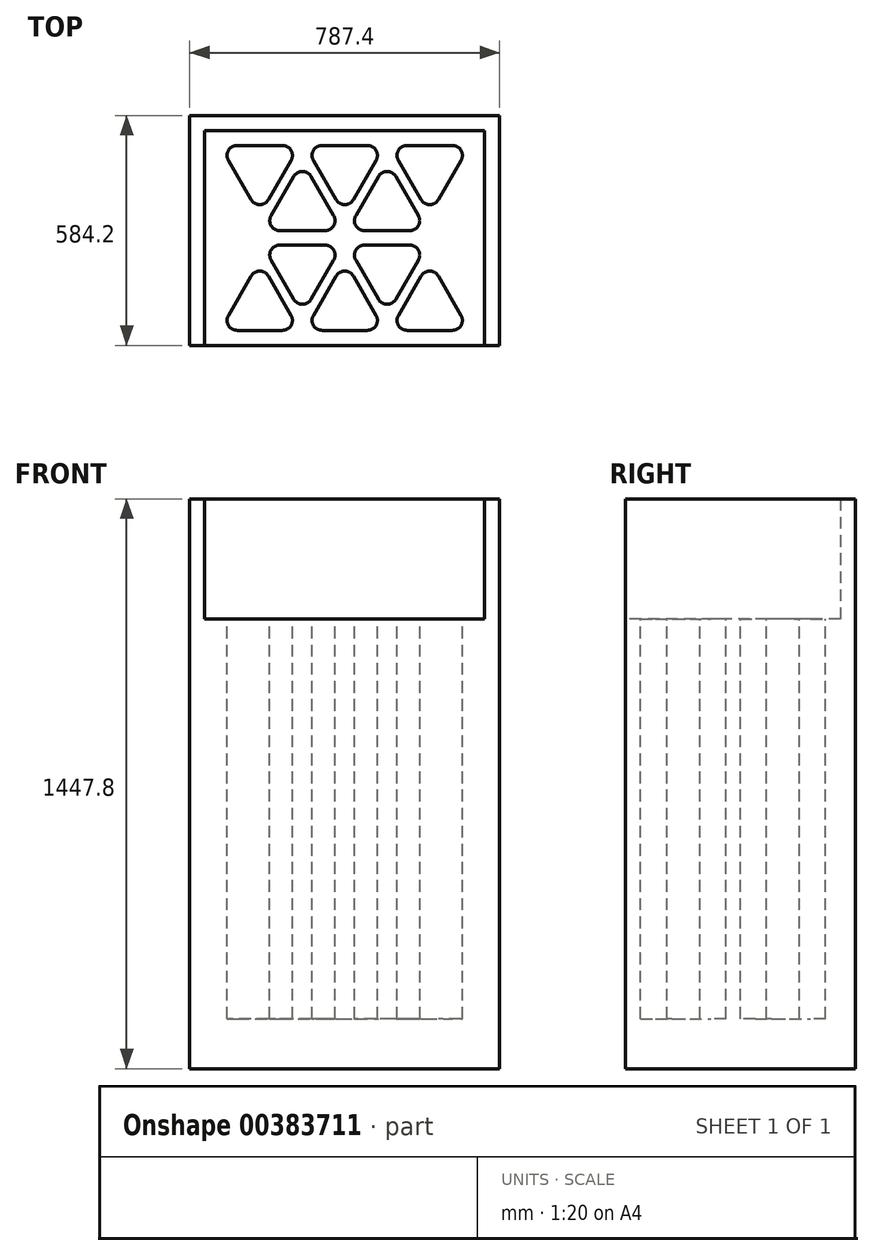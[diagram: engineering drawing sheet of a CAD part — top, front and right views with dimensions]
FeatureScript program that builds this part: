
annotation { "Feature Type Name" : "Feature", "Feature Type Description" : "" }
export const myFeature = defineFeature(function(context is Context, id is Id, definition is map)
    precondition{}
    {
        {
            var Q0;
            Q0=qCreatedBy(makeId("Top.planeOp"),FACE);
            var sketch = newSketch(context, id + "F0", { "sketchPlane" : qUnion([Q0])});
            skLineSegment(sketch, "E0.bottom", {"start": v(-70.95, -74.95) * mm, "end": v(716.45, -74.95) * mm});
            skLineSegment(sketch, "E0.top", {"start": v(-70.95, 509.25) * mm, "end": v(716.45, 509.25) * mm});
            skLineSegment(sketch, "E0.left", {"start": v(-70.95, -74.95) * mm, "end": v(-70.95, 509.25) * mm});
            skLineSegment(sketch, "E0.right", {"start": v(716.45, -74.95) * mm, "end": v(716.45, 509.25) * mm});
            skSolve(sketch);
        }
        {
            var Q0;
            Q0 = qSketchRegion(id + "F0", true);
            extrude(context, id + "F1", {"entities" : qUnion([Q0]), "depth" : 1447.8 * mm});
        }
        {
            var Q0;
            Q0=makeQuery(id+"F1.opExtrude","SWEPT_FACE",FACE,{"disambiguationData":[OSD([sQuery(id+"F0.wireOp",EDGE,"E0.bottom")])]});
            var sketch = newSketch(context, id + "F2", { "sketchPlane" : qUnion([Q0])});
            skLineSegment(sketch, "E1.bottom", {"start": v(-32.85, 1447.8) * mm, "end": v(678.35, 1447.8) * mm});
            skLineSegment(sketch, "E1.top", {"start": v(-32.85, 1143) * mm, "end": v(678.35, 1143) * mm});
            skLineSegment(sketch, "E1.left", {"start": v(-32.85, 1447.8) * mm, "end": v(-32.85, 1143) * mm});
            skLineSegment(sketch, "E1.right", {"start": v(678.35, 1447.8) * mm, "end": v(678.35, 1143) * mm});
            skSolve(sketch);
        }
        {
            var Q0;
            Q0 = qSketchRegion(id + "F2", true);
            extrude(context, id + "F3", {"entities" : qUnion([Q0]), "operationType" : NewBodyOperationType.REMOVE, "oppositeDirection" : true, "depth" : 546.1 * mm});
        }
        {
            var Q0;
            Q0=makeQuery(id+"F3.boolean.opBoolean","COPY",FACE,{"derivedFrom":makeQuery(id+"F3.opExtrude","SWEPT_FACE",FACE,{"disambiguationData":[OSD([sQuery(id+"F2.wireOp",EDGE,"E1.top")])]})});
            var sketch = newSketch(context, id + "F4", { "sketchPlane" : qUnion([Q0])});
            skLineSegment(sketch, "E2", {"start": v(49.24, -36.85) * mm, "end": v(164.45, -36.85) * mm});
            skLineSegment(sketch, "E3", {"start": v(186.45, 1.25) * mm, "end": v(128.84, 101.03) * mm});
            skLineSegment(sketch, "E4", {"start": v(84.85, 101.03) * mm, "end": v(27.24, 1.25) * mm});
            skPoint(sketch, "E5.visualSharp", {"position": v(106.85, 139.13) * mm});
            skArc(sketch, "E5.filletArc", {"start": v(128.84, 101.03) * mm, "mid": v(106.85, 113.73) * mm, "end": v(84.85, 101.03) * mm});
            skPoint(sketch, "E6.visualSharp", {"position": v(208.45, -36.85) * mm});
            skArc(sketch, "E6.filletArc", {"start": v(164.45, -36.85) * mm, "mid": v(186.45, -24.15) * mm, "end": v(186.45, 1.25) * mm});
            skPoint(sketch, "E7.visualSharp", {"position": v(5.25, -36.85) * mm});
            skArc(sketch, "E7.filletArc", {"start": v(27.24, 1.25) * mm, "mid": v(27.24, -24.15) * mm, "end": v(49.24, -36.85) * mm});
            skLineSegment(sketch, "E8.1.0.0", {"start": v(402.35, 1.25) * mm, "end": v(344.74, 101.03) * mm});
            skLineSegment(sketch, "E8.1.0.1", {"start": v(265.14, -36.85) * mm, "end": v(380.35, -36.85) * mm});
            skLineSegment(sketch, "E8.1.0.2", {"start": v(300.75, 101.03) * mm, "end": v(243.14, 1.25) * mm});
            skPoint(sketch, "E8.1.0.3", {"position": v(424.35, -36.85) * mm});
            skPoint(sketch, "E8.1.0.4", {"position": v(221.15, -36.85) * mm});
            skPoint(sketch, "E8.1.0.5", {"position": v(322.75, 139.13) * mm});
            skArc(sketch, "E8.1.0.6", {"start": v(344.74, 101.03) * mm, "mid": v(322.75, 113.73) * mm, "end": v(300.75, 101.03) * mm});
            skArc(sketch, "E8.1.0.7", {"start": v(380.35, -36.85) * mm, "mid": v(402.35, -24.15) * mm, "end": v(402.35, 1.25) * mm});
            skArc(sketch, "E8.1.0.8", {"start": v(243.14, 1.25) * mm, "mid": v(243.14, -24.15) * mm, "end": v(265.14, -36.85) * mm});
            skLineSegment(sketch, "E8.2.0.0", {"start": v(618.25, 1.25) * mm, "end": v(560.64, 101.03) * mm});
            skLineSegment(sketch, "E8.2.0.1", {"start": v(481.04, -36.85) * mm, "end": v(596.25, -36.85) * mm});
            skLineSegment(sketch, "E8.2.0.2", {"start": v(516.65, 101.03) * mm, "end": v(459.04, 1.25) * mm});
            skPoint(sketch, "E8.2.0.3", {"position": v(640.25, -36.85) * mm});
            skPoint(sketch, "E8.2.0.4", {"position": v(437.05, -36.85) * mm});
            skPoint(sketch, "E8.2.0.5", {"position": v(538.65, 139.13) * mm});
            skArc(sketch, "E8.2.0.6", {"start": v(560.64, 101.03) * mm, "mid": v(538.65, 113.73) * mm, "end": v(516.65, 101.03) * mm});
            skArc(sketch, "E8.2.0.7", {"start": v(596.25, -36.85) * mm, "mid": v(618.25, -24.15) * mm, "end": v(618.25, 1.25) * mm});
            skArc(sketch, "E8.2.0.8", {"start": v(459.04, 1.25) * mm, "mid": v(459.04, -24.15) * mm, "end": v(481.04, -36.85) * mm});
            skLineSegment(sketch, "E8.direction1", {"start": v(5.25, -36.85) * mm, "end": v(221.15, -36.85) * mm, "construction": true});
            skLineSegment(sketch, "E9", {"start": v(157.55, 179.9) * mm, "end": v(272.76, 179.9) * mm});
            skLineSegment(sketch, "E10", {"start": v(294.76, 141.8) * mm, "end": v(237.15, 42.02) * mm});
            skLineSegment(sketch, "E11", {"start": v(193.16, 42.02) * mm, "end": v(135.55, 141.8) * mm});
            skPoint(sketch, "E12.visualSharp", {"position": v(113.55, 179.9) * mm});
            skArc(sketch, "E12.filletArc", {"start": v(157.55, 179.9) * mm, "mid": v(135.55, 167.2) * mm, "end": v(135.55, 141.8) * mm});
            skPoint(sketch, "E13.visualSharp", {"position": v(316.75, 179.9) * mm});
            skArc(sketch, "E13.filletArc", {"start": v(294.76, 141.8) * mm, "mid": v(294.76, 167.2) * mm, "end": v(272.76, 179.9) * mm});
            skPoint(sketch, "E14.visualSharp", {"position": v(215.15, 3.92) * mm});
            skArc(sketch, "E14.filletArc", {"start": v(193.16, 42.02) * mm, "mid": v(215.15, 29.32) * mm, "end": v(237.15, 42.02) * mm});
            skLineSegment(sketch, "E15", {"start": v(322.75, 139.13) * mm, "end": v(322.75, 471.15) * mm, "construction": true});
            skArc(sketch, "E16.MirrorCS", {"start": v(487.94, 179.9) * mm, "mid": v(509.94, 167.2) * mm, "end": v(509.94, 141.8) * mm});
            skPoint(sketch, "E17.MirrorP", {"position": v(531.94, 179.9) * mm});
            skLineSegment(sketch, "E18.MirrorCS", {"start": v(452.34, 42.02) * mm, "end": v(509.94, 141.8) * mm});
            skArc(sketch, "E19.MirrorCS", {"start": v(452.34, 42.02) * mm, "mid": v(430.34, 29.32) * mm, "end": v(408.34, 42.02) * mm});
            skPoint(sketch, "E20.MirrorP", {"position": v(328.74, 179.9) * mm});
            skArc(sketch, "E21.MirrorCS", {"start": v(350.74, 141.8) * mm, "mid": v(350.74, 167.2) * mm, "end": v(372.73, 179.9) * mm});
            skLineSegment(sketch, "E22.MirrorCS", {"start": v(350.74, 141.8) * mm, "end": v(408.34, 42.02) * mm});
            skPoint(sketch, "E23.MirrorP", {"position": v(430.34, 3.92) * mm});
            skLineSegment(sketch, "E24.MirrorCS", {"start": v(487.94, 179.9) * mm, "end": v(372.73, 179.9) * mm});
            skLineSegment(sketch, "E25.MirrorCS", {"start": v(49.24, 433.05) * mm, "end": v(164.45, 433.05) * mm});
            skPoint(sketch, "E26.MirrorP", {"position": v(106.85, 257.07) * mm});
            skPoint(sketch, "E27.MirrorP", {"position": v(531.94, 216.3) * mm});
            skLineSegment(sketch, "E28.MirrorCS", {"start": v(618.25, 394.95) * mm, "end": v(560.64, 295.17) * mm});
            skArc(sketch, "E29.MirrorCS", {"start": v(193.16, 354.18) * mm, "mid": v(215.15, 366.88) * mm, "end": v(237.15, 354.18) * mm});
            skLineSegment(sketch, "E30.MirrorCS", {"start": v(481.04, 433.05) * mm, "end": v(596.25, 433.05) * mm});
            skLineSegment(sketch, "E31.MirrorCS", {"start": v(350.74, 254.4) * mm, "end": v(408.34, 354.18) * mm});
            skLineSegment(sketch, "E32.MirrorCS", {"start": v(193.16, 354.18) * mm, "end": v(135.55, 254.4) * mm});
            skPoint(sketch, "E33.MirrorP", {"position": v(640.25, 433.05) * mm});
            skArc(sketch, "E34.MirrorCS", {"start": v(452.34, 354.18) * mm, "mid": v(430.34, 366.88) * mm, "end": v(408.34, 354.18) * mm});
            skArc(sketch, "E35.MirrorCS", {"start": v(243.14, 394.95) * mm, "mid": v(243.14, 420.35) * mm, "end": v(265.14, 433.05) * mm});
            skArc(sketch, "E36.MirrorCS", {"start": v(157.55, 216.3) * mm, "mid": v(135.55, 229) * mm, "end": v(135.55, 254.4) * mm});
            skLineSegment(sketch, "E37.MirrorCS", {"start": v(487.94, 216.3) * mm, "end": v(372.73, 216.3) * mm});
            skArc(sketch, "E38.MirrorCS", {"start": v(380.35, 433.05) * mm, "mid": v(402.35, 420.35) * mm, "end": v(402.35, 394.95) * mm});
            skLineSegment(sketch, "E39.MirrorCS", {"start": v(5.25, 433.05) * mm, "end": v(221.15, 433.05) * mm, "construction": true});
            skArc(sketch, "E40.MirrorCS", {"start": v(344.74, 295.17) * mm, "mid": v(322.75, 282.47) * mm, "end": v(300.75, 295.17) * mm});
            skPoint(sketch, "E41.MirrorP", {"position": v(221.15, 433.05) * mm});
            skLineSegment(sketch, "E42.MirrorCS", {"start": v(300.75, 295.17) * mm, "end": v(243.14, 394.95) * mm});
            skPoint(sketch, "E43.MirrorP", {"position": v(424.35, 433.05) * mm});
            skPoint(sketch, "E44.MirrorP", {"position": v(215.15, 392.28) * mm});
            skArc(sketch, "E45.MirrorCS", {"start": v(487.94, 216.3) * mm, "mid": v(509.94, 229) * mm, "end": v(509.94, 254.4) * mm});
            skLineSegment(sketch, "E46.MirrorCS", {"start": v(265.14, 433.05) * mm, "end": v(380.35, 433.05) * mm});
            skLineSegment(sketch, "E47.MirrorCS", {"start": v(157.55, 216.3) * mm, "end": v(272.76, 216.3) * mm});
            skLineSegment(sketch, "E48.MirrorCS", {"start": v(402.35, 394.95) * mm, "end": v(344.74, 295.17) * mm});
            skPoint(sketch, "E49.MirrorP", {"position": v(322.75, 257.07) * mm});
            skArc(sketch, "E50.MirrorCS", {"start": v(27.24, 394.95) * mm, "mid": v(27.24, 420.35) * mm, "end": v(49.24, 433.05) * mm});
            skArc(sketch, "E51.MirrorCS", {"start": v(164.45, 433.05) * mm, "mid": v(186.45, 420.35) * mm, "end": v(186.45, 394.95) * mm});
            skArc(sketch, "E52.MirrorCS", {"start": v(128.84, 295.17) * mm, "mid": v(106.85, 282.47) * mm, "end": v(84.85, 295.17) * mm});
            skPoint(sketch, "E53.MirrorP", {"position": v(208.45, 433.05) * mm});
            skPoint(sketch, "E54.MirrorP", {"position": v(113.55, 216.3) * mm});
            skLineSegment(sketch, "E55.MirrorCS", {"start": v(84.85, 295.17) * mm, "end": v(27.24, 394.95) * mm});
            skArc(sketch, "E56.MirrorCS", {"start": v(294.76, 254.4) * mm, "mid": v(294.76, 229) * mm, "end": v(272.76, 216.3) * mm});
            skPoint(sketch, "E57.MirrorP", {"position": v(328.74, 216.3) * mm});
            skLineSegment(sketch, "E58.MirrorCS", {"start": v(186.45, 394.95) * mm, "end": v(128.84, 295.17) * mm});
            skArc(sketch, "E59.MirrorCS", {"start": v(596.25, 433.05) * mm, "mid": v(618.25, 420.35) * mm, "end": v(618.25, 394.95) * mm});
            skLineSegment(sketch, "E60.MirrorCS", {"start": v(452.34, 354.18) * mm, "end": v(509.94, 254.4) * mm});
            skPoint(sketch, "E61.MirrorP", {"position": v(538.65, 257.07) * mm});
            skArc(sketch, "E62.MirrorCS", {"start": v(350.74, 254.4) * mm, "mid": v(350.74, 229) * mm, "end": v(372.73, 216.3) * mm});
            skLineSegment(sketch, "E63.MirrorCS", {"start": v(294.76, 254.4) * mm, "end": v(237.15, 354.18) * mm});
            skPoint(sketch, "E64.MirrorP", {"position": v(430.34, 392.28) * mm});
            skArc(sketch, "E65.MirrorCS", {"start": v(560.64, 295.17) * mm, "mid": v(538.65, 282.47) * mm, "end": v(516.65, 295.17) * mm});
            skPoint(sketch, "E66.MirrorP", {"position": v(316.75, 216.3) * mm});
            skPoint(sketch, "E67.MirrorP", {"position": v(5.25, 433.05) * mm});
            skPoint(sketch, "E68.MirrorP", {"position": v(437.05, 433.05) * mm});
            skArc(sketch, "E69.MirrorCS", {"start": v(459.04, 394.95) * mm, "mid": v(459.04, 420.35) * mm, "end": v(481.04, 433.05) * mm});
            skLineSegment(sketch, "E70.MirrorCS", {"start": v(516.65, 295.17) * mm, "end": v(459.04, 394.95) * mm});
            skLineSegment(sketch, "E71", {"start": v(-32.85, 198.1) * mm, "end": v(678.35, 198.1) * mm, "construction": true});
            skSolve(sketch);
        }
        {
            var Q0;
            Q0 = qSketchRegion(id + "F4", true);
            extrude(context, id + "F5", {"entities" : qUnion([Q0]), "operationType" : NewBodyOperationType.REMOVE, "oppositeDirection" : true, "depth" : 1016 * mm});
        }
    });
